# Revit family: HERZ-DR-T-90 Radiator Control Valve Angle Model 6824
name_source: partatom
category: Rohrzubehör
units: mm (PartAtom-declared; Revit-internal decimal feet)

## family parameters
Arbeitsebenenbasiert = Nein
Beim Laden mit Abzugskörper schneiden = Nein
Bemaßung runder Anschluss = Durchmesser verwenden
Gemeinsam genutzt = Nein
Immer vertikal = Ja
OmniClass-Nummer = 23.65.55.14
OmniClass-Titel = Valves for Liquid Services
Teiletyp = Unterbricht

## types (1)
- HERZ-DR-T-90 Radiator Control Valve Angle Model 6824
    Application = Hot Water Heating Systems
Where high-precision adjustment and minimum cost are required.
Installation in air conditioning systems for exact adjustment of cooling and heating units, also suitable ascircuit control valves.
    Body = nickel plated
    Hand wheel = plastic, white
    Hersteller = HERZ Armaturen Ges.m.b.H.
    Max. operating pressure = 1000000.0 Pa
    Max. operating temperature = 110 °C
    Medium = Hot water quality according to Austrian standard ÖNORM H 5195 and/or VDI-guideline 2035.
    Model = All models are nickel plated, with white screw disk, handwheel protection caps.
    R01 = 10.75 mm  [stored 0.035269 ft]
    S01 = 10 mm  [stored 0.0328084 ft]
    S04 = 45 mm  [stored 0.147638 ft]
    SCRNCODE = 05;00;02
    SCRNSEQ = ARM;ARM_TYP="ALLF";2
    URL = www.herzvalves.com
    Vorgabe-Ansicht = 0 mm  [stored 0 ft]

note: [stored X ft] marks values corroborated as IEEE doubles in the binary element streams (Revit-internal decimal feet)
